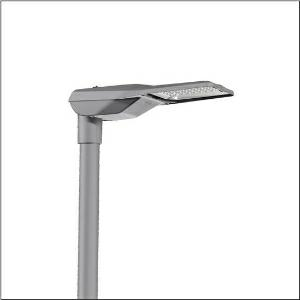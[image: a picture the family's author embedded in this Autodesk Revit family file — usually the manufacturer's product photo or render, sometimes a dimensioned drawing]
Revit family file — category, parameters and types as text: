
# Revit family: streetlight_sl_21_iq_mini___st1_0ab_5xe2m31v08hb_1211
name_source: partatom
category: Lighting Fixtures
units: mm (PartAtom-declared; Revit-internal decimal feet)

## family parameters
Cut with Voids When Loaded = No
Host = Face
Light Source = No
Part Type = Normal
Room Calculation Point = No
Round Connector Dimension = Use Diameter
Shared = No

## types (1)
- --- (1 x LED, 8580 lm, 71 W, 3000K)
    Apparent Load = 71 VA
    CIE Flux Codes = 38 73 97 100 100
    Color Rendering = 70
    Color Temperature = 3000K
    Default Elevation = 1800 mm
    Description = Streetlight SL 21 iQ mini, mast luminaire, primary light control with lens, of PMMA, primary optical cover: cover, of toughened safety glass, transparent, light distribution: ST1.0aB, light emission: direct distribution, primary light characteristic: asymmetric, installation type: post-top, side-entry, LED, High Power LED, rated luminous flux: 8.580lm, luminous efficacy: 121lm/W, light colour: 730, colour temperature: 3000K, control gear: iQ-Street Remote, D4i with power reduction, control: pre-setting: logarithmic dimming characteristic, Street-Remote, Auto-Match, Temp-Guard, Lumen-Switch, Night-Set, Smart-Wire, Light-Fading, Desk-Remote (wireless, voltage-free reading and setting of iQ features in the workshop via application-optimized NFC function/RFID function), optimised constant luminous flux control (CLO 2.0), mains connection: 220..240V, AC, 50/60Hz, start of lifetime: 71W, end of service life: 75W, reduction: 30W, luminaire housing, of diecast aluminium, powder-coated, Siteco® metallic grey (DB 702S), corrosivity category C5 mid according to DIN EN ISO 12944, please order mast flange separately, inclination adjustable: 0°, 5°, 10°, 15°, sealing non-destructively replaceable, multi-level sealing system, length: 628mm, width: 235mm, height: 110mm, mast flange for spigot size: 42mm (side-entry): 5XC10008XM4, 60/48mm (side-entry/post-top): 5XC10108XM2, 76/60mm (side-entry/post-top): 5XC10108XM1, mounting height: 4..8m, Smart Interface above, protection rating (complete): IP66, insulation class (complete): insulation class II (safety insulation), certification: CE, ENEC, ENEC+, VDE, impact resistance: IK10, permissible operating ambient temperature for outdoor applications: -40..+50°C, standard-compliant lighting for roads and squares, packaging unit: 1 piece

Light Distribution: ST1.0aB
    Height = 110 mm
    Lamp = 1 x LED
    Lamp Light Flux = 8580 lm
    Lamp Power = 71 W
    Lamp count = 1
    Length = 625 mm
    Luminous efficacy = 121 lm/W
    Manufacturer = Siteco
    ModVariant = No
    Model = 5XE2M31V08HB
    Number of Poles = 1
    OnlyDefault = Yes
    Power Factor = 1
    Product Name = Streetlight SL 21 iQ mini | ST1.0aB
    Product group = mast luminaire | pylon top
    ProductGroupID = 6100
    Protection Class = Protection class II
    Protection Degree = IP 66
    RLX_Detail_Level = 1
    RLX_Emergency_Light_Flux = 0 lm
    RLX_Emergency_Type = 0
    RLX_Emergency_Type_DB = No
    RlxData = <blob elided: 26473 chars, md5=768231a3>
    Socket = socket
    Standby Power = 0 W
    System Light Flux = 8580 lm
    System Power = 71 W
    Type Comments = factory setting: luminous flux: 100 % | dim-lin: 254 | 716 mA
    Type Image = l_1003515.jpg
    URL = http://relux.com
    VarID = @adj_112478
    Voltage = 0 V
    Weight = 0.00 kg
    Width = 234 mm

## geometry (parser evidence)
native form markers: Blend x4, Sweep x10
no freeform markers — native parametric forms only
